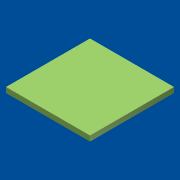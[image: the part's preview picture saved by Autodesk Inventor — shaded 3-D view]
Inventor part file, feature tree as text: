
AUTODESK INVENTOR PART (.ipt)
format: ipt  version: 2014 (Build 180170000, 170)  size: 98,816 bytes
history: native  units: in
note: dims shown in document units (in); Inventor stores cm internally (conversion verified against a paired STEP export)
features: extrude x1, sketch x1
ambient origin geometry x8: Origin, YZ Plane, XZ Plane, XY Plane, X Axis, Y Axis, Z Axis, Center Point
bodies: Solid1 (feature_tree)
feature tree (2):
  extrude  "Extrusion1"  Depth=8.0in
  sketch  "SketchTable"  dims[d0=8.0in d1=8.0in d2=0.5in d3=0.0in]
